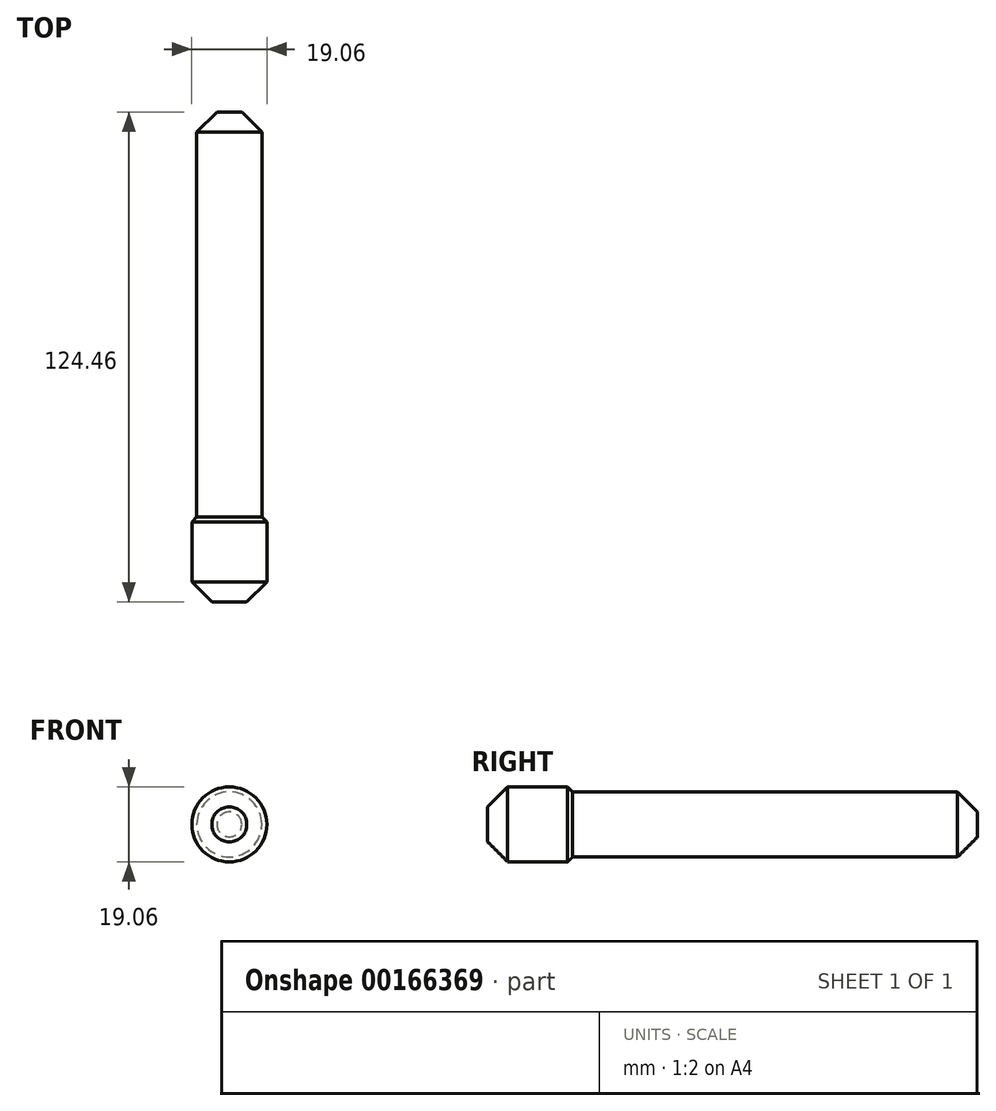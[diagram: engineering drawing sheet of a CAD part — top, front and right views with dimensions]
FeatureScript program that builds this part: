
annotation { "Feature Type Name" : "Feature", "Feature Type Description" : "" }
export const myFeature = defineFeature(function(context is Context, id is Id, definition is map)
    precondition{}
    {
        {
            var Q0;
            Q0=qCreatedBy(makeId("Front.planeOp"),FACE);
            var sketch = newSketch(context, id + "F0", { "sketchPlane" : qUnion([Q0])});
            skCircle(sketch, "E0", {"center": v(0, 0) * mm, "radius": 8.26 * mm});
            skSolve(sketch);
        }
        {
            var Q0;
            Q0 = qSketchRegion(id + "F0", true);
            extrude(context, id + "F1", {"entities" : qUnion([Q0]), "depth" : 99.06 * mm});
        }
        {
            var Q0;
            Q0=makeQuery(id+"F1.opExtrude","CAP_FACE",FACE,{"disambiguationData":[OSD([sQuery(id+"F0.wireOp",EDGE,"E0")])],"isStart":false});
            var sketch = newSketch(context, id + "F2", { "sketchPlane" : qUnion([Q0])});
            skCircle(sketch, "E1", {"center": v(0, 0) * mm, "radius": 9.53 * mm});
            skSolve(sketch);
        }
        {
            var Q0;
            Q0 = qSketchRegion(id + "F2", true);
            extrude(context, id + "F3", {"entities" : qUnion([Q0]), "operationType" : NewBodyOperationType.ADD, "depth" : 25.4 * mm});
        }
        {
            var Q0;
            Q0=makeQuery(id+"F3.opExtrude","SWEPT_FACE",FACE,{"disambiguationData":[OSD([sQuery(id+"F2.wireOp",EDGE,"E1")])]});
            chamfer(context, id + "F4", {"entities" : qUnion([Q0]), "width" : 5.08 * mm, "tangentPropagation" : true});
        }
        {
            var Q0;
            Q0=makeQuery(id+"F1.opExtrude","CAP_FACE",FACE,{"disambiguationData":[OSD([sQuery(id+"F0.wireOp",EDGE,"E0")])],"isStart":true});
            chamfer(context, id + "F5", {"entities" : qUnion([Q0]), "width" : 5.08 * mm, "tangentPropagation" : true});
        }
    });
